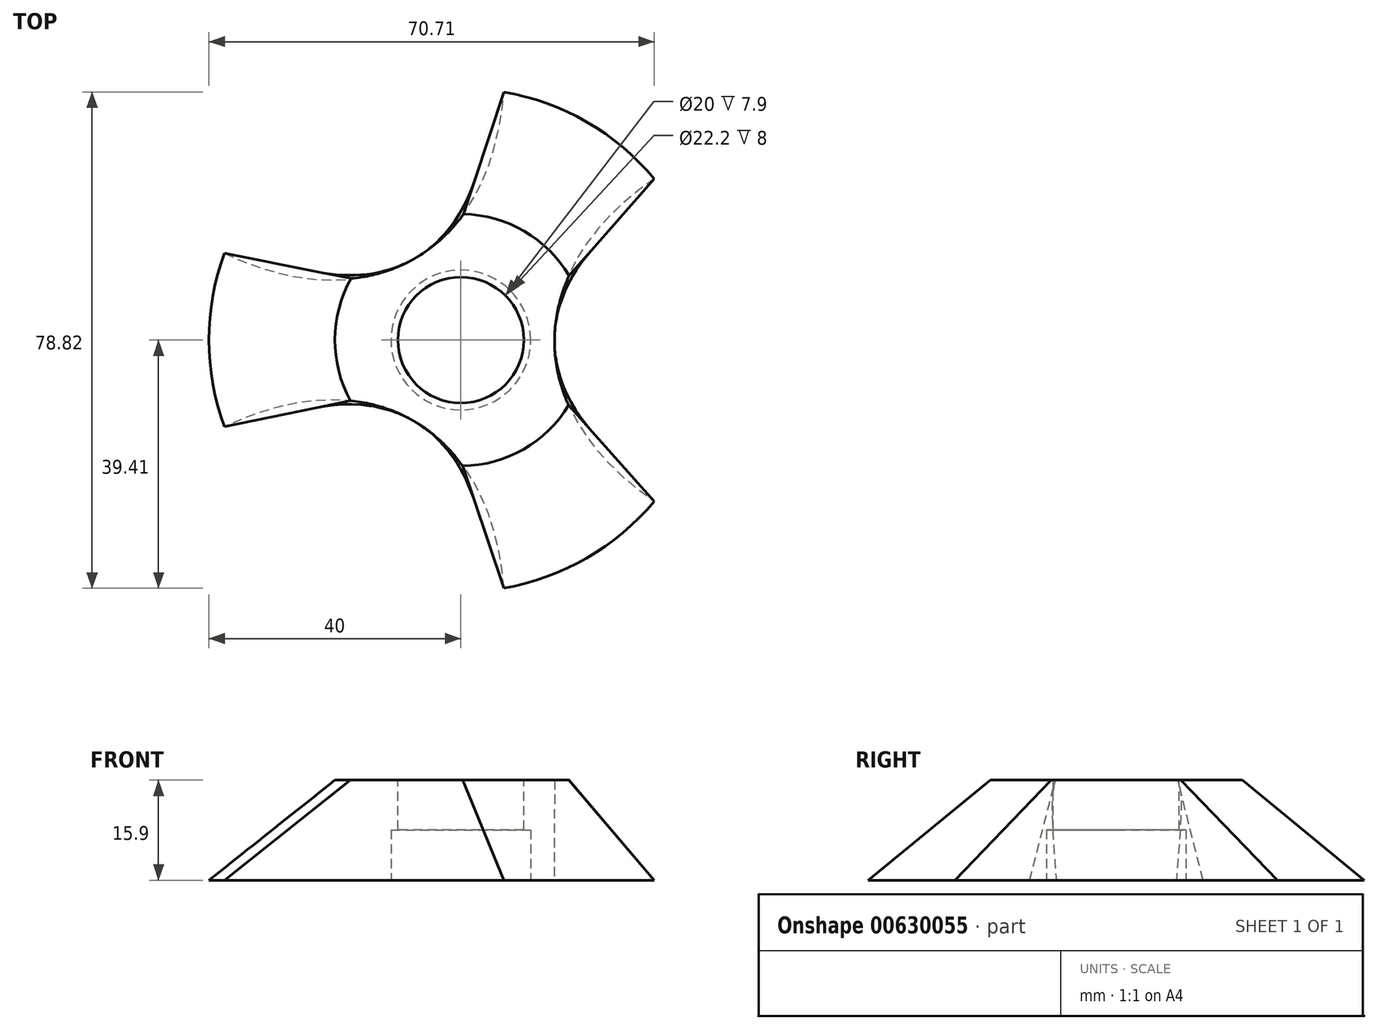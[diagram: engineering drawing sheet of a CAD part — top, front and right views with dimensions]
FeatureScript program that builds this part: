
annotation { "Feature Type Name" : "Feature", "Feature Type Description" : "" }
export const myFeature = defineFeature(function(context is Context, id is Id, definition is map)
    precondition{}
    {
        {
            var Q0;
            Q0=qCreatedBy(makeId("Top.planeOp"),FACE);
            var sketch = newSketch(context, id + "F0", { "sketchPlane" : qUnion([Q0])});
            skCircle(sketch, "E0", {"center": v(0, 0) * mm, "radius": 40 * mm});
            skEllipticalArc(sketch, "E1", {});
            skEllipticalArc(sketch, "E2.1.0", {});
            skEllipticalArc(sketch, "E2.2.0", {});
            const initialGuessF0  = {"E1": [0.07511108368634757, 0, 1, 0, 0.060275472700595856, 0.03788497461421287, 2.3987646426329534, 3.8844206645464987], "E2.1.0": [-0.03755554184318008, 0.06504810657815958, -0.5, 0.8660254037844388, 0.060275472700595856, 0.03788497461421287, 2.398764642632954, 3.884420664546499], "E2.2.0": [-0.03755554184318008, -0.06504810657815956, -0.5, -0.8660254037844387, 0.060275472700595856, 0.03788497461421287, 2.398764642632954, 3.884420664546499]};
            skSetInitialGuess(sketch, initialGuessF0);
            skSolve(sketch);
        }
        {
            var Q0;
            Q0=qCreatedBy(makeId("Top.planeOp"),FACE);
            cPlane(context, id + "F1", {"entities" : qUnion([Q0]), "cplaneType" : CPlaneType.OFFSET, "offset" : 15.9 * mm, "width" : 150 * mm, "height" : 150 * mm});
        }
        {
            var Q0;
            Q0=qCreatedBy(id+"F1.planeOp",FACE);
            var sketch = newSketch(context, id + "F2", { "sketchPlane" : qUnion([Q0])});
            skCircle(sketch, "E3", {"center": v(0, 0) * mm, "radius": 20 * mm});
            skEllipticalArc(sketch, "E4", {});
            skEllipticalArc(sketch, "E5.1.0", {});
            skEllipticalArc(sketch, "E5.2.0", {});
            skPoint(sketch, "E6.orphan", {"position": v(-37.44, 13.9) * mm});
            skPoint(sketch, "E7.orphan", {"position": v(-37.7, -13.75) * mm});
            skPoint(sketch, "E8.orphan", {"position": v(6.68, -39.37) * mm});
            skPoint(sketch, "E9.orphan", {"position": v(30.76, -25.78) * mm});
            skPoint(sketch, "E10.orphan", {"position": v(30.76, 25.47) * mm});
            skPoint(sketch, "E11.orphan", {"position": v(6.95, 39.53) * mm});
            const initialGuessF2  = {"E4": [0.0751548633301423, -0.00015633105500385694, 1, 0, 0.060275472700595856, 0.03788497461421287, 2.8639645145277646, 3.4143156120066758], "E5.1.0": [-0.03744204500003737, 0.06516418638935272, -0.5, 0.8660254037844388, 0.060275472700595856, 0.03788497461421287, 2.8639645145277646, 3.414315612006676], "E5.2.0": [-0.03771281833010495, -0.06500785533434884, -0.5, -0.8660254037844384, 0.060275472700595856, 0.03788497461421287, 2.863964514527765, 3.4143156120066758]};
            skSetInitialGuess(sketch, initialGuessF2);
            skSolve(sketch);
        }
        {
            var Q0;
            {var subQ0=sQuery(id+"F0.wireOp",EDGE,"E1");Q0=makeQuery(id+"F0.imprint","IMPRINT",FACE,{"disambiguationData":[TD([[makeQuery(id+"F0.imprint","IMPRINT",EDGE,{"derivedFrom":subQ0}),-1.0]])]});}
            var Q1;
            {var subQ0=sQuery(id+"F2.wireOp",EDGE,"E4");Q1=makeQuery(id+"F2.imprint","IMPRINT",FACE,{"disambiguationData":[TD([[makeQuery(id+"F2.imprint","IMPRINT",EDGE,{"derivedFrom":subQ0}),-1.0]])]});}
            loft(context, id + "F3", {"sheetProfilesArray" : [{ "sheetProfileEntities" : qUnion([Q0]) }, { "sheetProfileEntities" : qUnion([Q1]) }]});
        }
        {
            var Q0;
            {var subQ0=sQuery(id+"F2.wireOp",EDGE,"E4");Q0=makeQuery(id+"F3.opLoft","CAP_FACE",FACE,{"disambiguationData":[OSD([makeQuery(id+"F2.imprint","IMPRINT",FACE,{"disambiguationData":[TD([[makeQuery(id+"F2.imprint","IMPRINT",EDGE,{"derivedFrom":subQ0}),-1.0]])]})])],"isStart":true});}
            var sketch = newSketch(context, id + "F4", { "sketchPlane" : qUnion([Q0])});
            skCircle(sketch, "E12", {"center": v(0, 0) * mm, "radius": 10 * mm});
            skSolve(sketch);
        }
        {
            var Q0;
            Q0 = qSketchRegion(id + "F4", true);
            extrude(context, id + "F5", {"entities" : qUnion([Q0]), "operationType" : NewBodyOperationType.REMOVE, "oppositeDirection" : true, "depth" : 25 * mm, "offsetDistance" : 25 * mm});
        }
        {
            var Q0;
            {var subQ0=sQuery(id+"F0.wireOp",EDGE,"E1");Q0=makeQuery(id+"F3.opLoft","CAP_FACE",FACE,{"disambiguationData":[OSD([makeQuery(id+"F0.imprint","IMPRINT",FACE,{"disambiguationData":[TD([[makeQuery(id+"F0.imprint","IMPRINT",EDGE,{"derivedFrom":subQ0}),-1.0]])]})])],"isStart":true});}
            var sketch = newSketch(context, id + "F6", { "sketchPlane" : qUnion([Q0])});
            skCircle(sketch, "E13", {"center": v(0, 0) * mm, "radius": 11.1 * mm});
            skSolve(sketch);
        }
        {
            var Q0;
            Q0=makeQuery(id+"F6.imprint","IMPRINT",FACE,{"disambiguationData":[TD([[makeQuery(id+"F6.imprint","IMPRINT",EDGE,{"derivedFrom":sQuery(id+"F6.wireOp",EDGE,"E13")}),1.0]])]});
            extrude(context, id + "F7", {"entities" : qUnion([Q0]), "operationType" : NewBodyOperationType.REMOVE, "oppositeDirection" : true, "depth" : 8 * mm, "offsetDistance" : 25 * mm});
        }
    });
